# Revit family: Door_Frame_Protector-Construction_Specialties
name_source: partatom
category: Specialty Equipment
revit_build: Autodesk Revit 2017 (Build: 20160225_1515(x64)
units: mm (PartAtom-declared; Revit-internal decimal feet)

## family parameters
Always vertical = Yes
Cut with Voids When Loaded = No
OmniClass Number = 23.30.10.11.34
OmniClass Title = Door Accessories
Part Type = Normal
Room Calculation Point = No
Round Connector Dimension = Use Diameter
Shared = Yes
Work Plane-Based = No

## types (7) — shared parameters

## per-type parameters (varying)
| type | Assembly Code | Description | Manufacturer | Model | No DFP | Product Documentation Link | Product Page URL | URL |
| None |  |  |  |  | Yes |  |  |  |
| A1-DFPN | C1020410 | Acrovyn Door Frame Protection | Construction Specialties | A1-DFPN | No | https://www.c-sgroup.com | https://www.c-sgroup.com | https://www.c-sgroup.com |
| A2-DFPN | C1020410 | Acrovyn Door Frame Protection | Construction Specialties | A2-DFPN | No | https://www.c-sgroup.com | https://www.c-sgroup.com | https://www.c-sgroup.com |
| B1-DFPN | C1020410 | Acrovyn Door Frame Protection | Construction Specialties | B1-DFPN | No | https://www.c-sgroup.com | https://www.c-sgroup.com | https://www.c-sgroup.com |
| B2-DFPN | C1020410 | Acrovyn Door Frame Protection | Construction Specialties | B2-DFPN | No | https://www.c-sgroup.com | https://www.c-sgroup.com | https://www.c-sgroup.com |
| D1-DFPN | C1020410 | Acrovyn Door Frame Protection | Construction Specialties | D1-DFPN | No | https://www.c-sgroup.com | https://www.c-sgroup.com | https://www.c-sgroup.com |
| D2-DFPN | C1020410 | Acrovyn Door Frame Protection | Construction Specialties | D2-DFPN | No | https://www.c-sgroup.com | https://www.c-sgroup.com | https://www.c-sgroup.com |

## geometry (parser evidence)
native form markers: Sweep x2
no freeform markers — native parametric forms only
